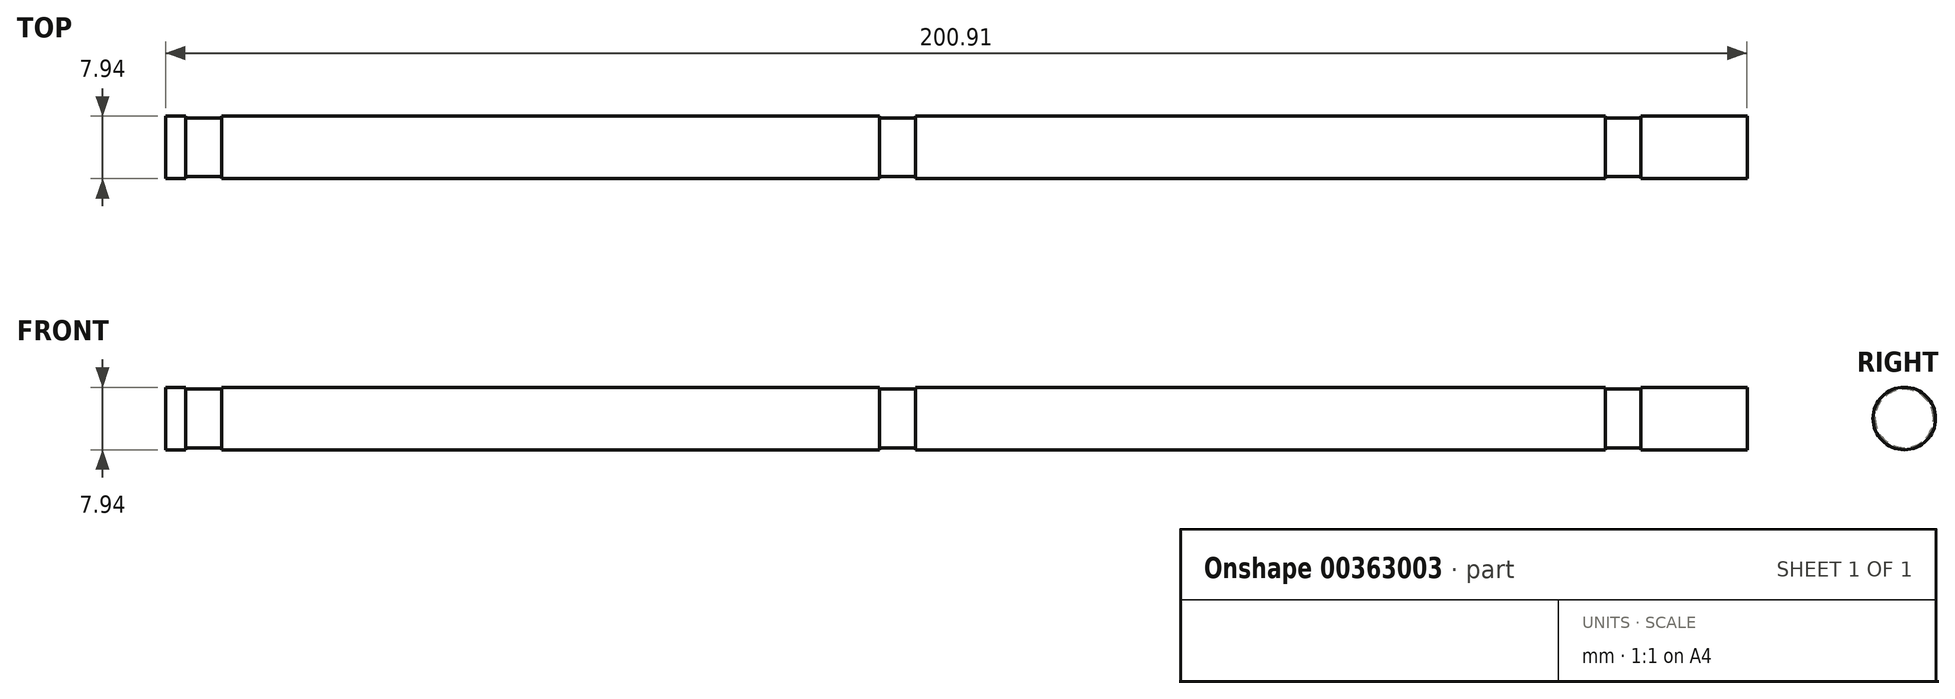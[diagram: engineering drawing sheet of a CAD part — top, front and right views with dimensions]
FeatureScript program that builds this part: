
annotation { "Feature Type Name" : "Feature", "Feature Type Description" : "" }
export const myFeature = defineFeature(function(context is Context, id is Id, definition is map)
    precondition{}
    {
        {
            var Q0;
            Q0=qCreatedBy(makeId("Right.planeOp"),FACE);
            var sketch = newSketch(context, id + "F0", { "sketchPlane" : qUnion([Q0])});
            skCircle(sketch, "E0", {"center": v(0, 0) * mm, "radius": 3.97 * mm});
            skSolve(sketch);
        }
        {
            var Q0;
            Q0=makeQuery(id+"F0.imprint","IMPRINT",FACE,{"disambiguationData":[TD([[makeQuery(id+"F0.imprint","IMPRINT",EDGE,{"derivedFrom":sQuery(id+"F0.wireOp",EDGE,"E0")}),1.0]])]});
            extrude(context, id + "F1", {"entities" : qUnion([Q0]), "depth" : 200.9 * mm});
        }
        {
            var Q0;
            Q0=qCreatedBy(makeId("Front.planeOp"),FACE);
            var sketch = newSketch(context, id + "F2", { "sketchPlane" : qUnion([Q0])});
            skLineSegment(sketch, "E1", {"start": v(200.91, -3.97) * mm, "end": v(0, -3.97) * mm});
            skLineSegment(sketch, "E2", {"start": v(-3.92, 0) * mm, "end": v(200.91, 0) * mm});
            skLineSegment(sketch, "E3", {"start": v(2.54, 3.97) * mm, "end": v(7.11, 3.97) * mm});
            skLineSegment(sketch, "E4.0", {"start": v(2.54, 3.72) * mm, "end": v(7.11, 3.72) * mm});
            skLineSegment(sketch, "E5.0", {"start": v(7.11, 3.97) * mm, "end": v(7.11, 3.72) * mm});
            skLineSegment(sketch, "E6.0", {"start": v(2.54, 3.97) * mm, "end": v(2.54, 3.72) * mm});
            skLineSegment(sketch, "E7.0", {"start": v(90.68, 3.97) * mm, "end": v(90.68, 3.72) * mm});
            skLineSegment(sketch, "E8.0", {"start": v(95.25, 3.97) * mm, "end": v(95.25, 3.72) * mm});
            skLineSegment(sketch, "E9", {"start": v(200.91, 3.97) * mm, "end": v(200.91, 0) * mm});
            skLineSegment(sketch, "E10.0", {"start": v(182.88, 3.97) * mm, "end": v(182.88, 3.72) * mm});
            skLineSegment(sketch, "E11.0", {"start": v(187.45, 3.97) * mm, "end": v(187.45, 3.72) * mm});
            skLineSegment(sketch, "E12.trimOffspring", {"start": v(182.88, 3.97) * mm, "end": v(187.45, 3.97) * mm});
            skLineSegment(sketch, "E13.trimOffspring", {"start": v(182.88, 3.72) * mm, "end": v(187.45, 3.72) * mm});
            skLineSegment(sketch, "E14.trimOffspring", {"start": v(90.68, 3.97) * mm, "end": v(95.25, 3.97) * mm});
            skLineSegment(sketch, "E15.trimOffspring", {"start": v(90.68, 3.72) * mm, "end": v(95.25, 3.72) * mm});
            skSolve(sketch);
        }
        {
            var Q0;
            Q0=makeQuery(id+"F2.imprint","IMPRINT",FACE,{"disambiguationData":[TD([[makeQuery(id+"F2.imprint","IMPRINT",EDGE,{"derivedFrom":sQuery(id+"F2.wireOp",EDGE,"E10.0")}),1.0]])]});
            var Q1;
            Q1=makeQuery(id+"F2.imprint","IMPRINT",FACE,{"disambiguationData":[TD([[makeQuery(id+"F2.imprint","IMPRINT",EDGE,{"derivedFrom":sQuery(id+"F2.wireOp",EDGE,"E7.0")}),1.0]])]});
            var Q2;
            Q2=makeQuery(id+"F2.imprint","IMPRINT",FACE,{"disambiguationData":[TD([[makeQuery(id+"F2.imprint","IMPRINT",EDGE,{"derivedFrom":sQuery(id+"F2.wireOp",EDGE,"E3")}),-1.0]])]});
            var Q3;
            Q3=sQuery(id+"F2.wireOp",EDGE,"E2");
            revolve(context, id + "F3", {"operationType" : NewBodyOperationType.REMOVE, "entities" : qUnion([Q0, Q1, Q2]), "axis" : qUnion([Q3]), "revolveType" : RevolveType.FULL, "oppositeDirection" : true});
        }
    });
